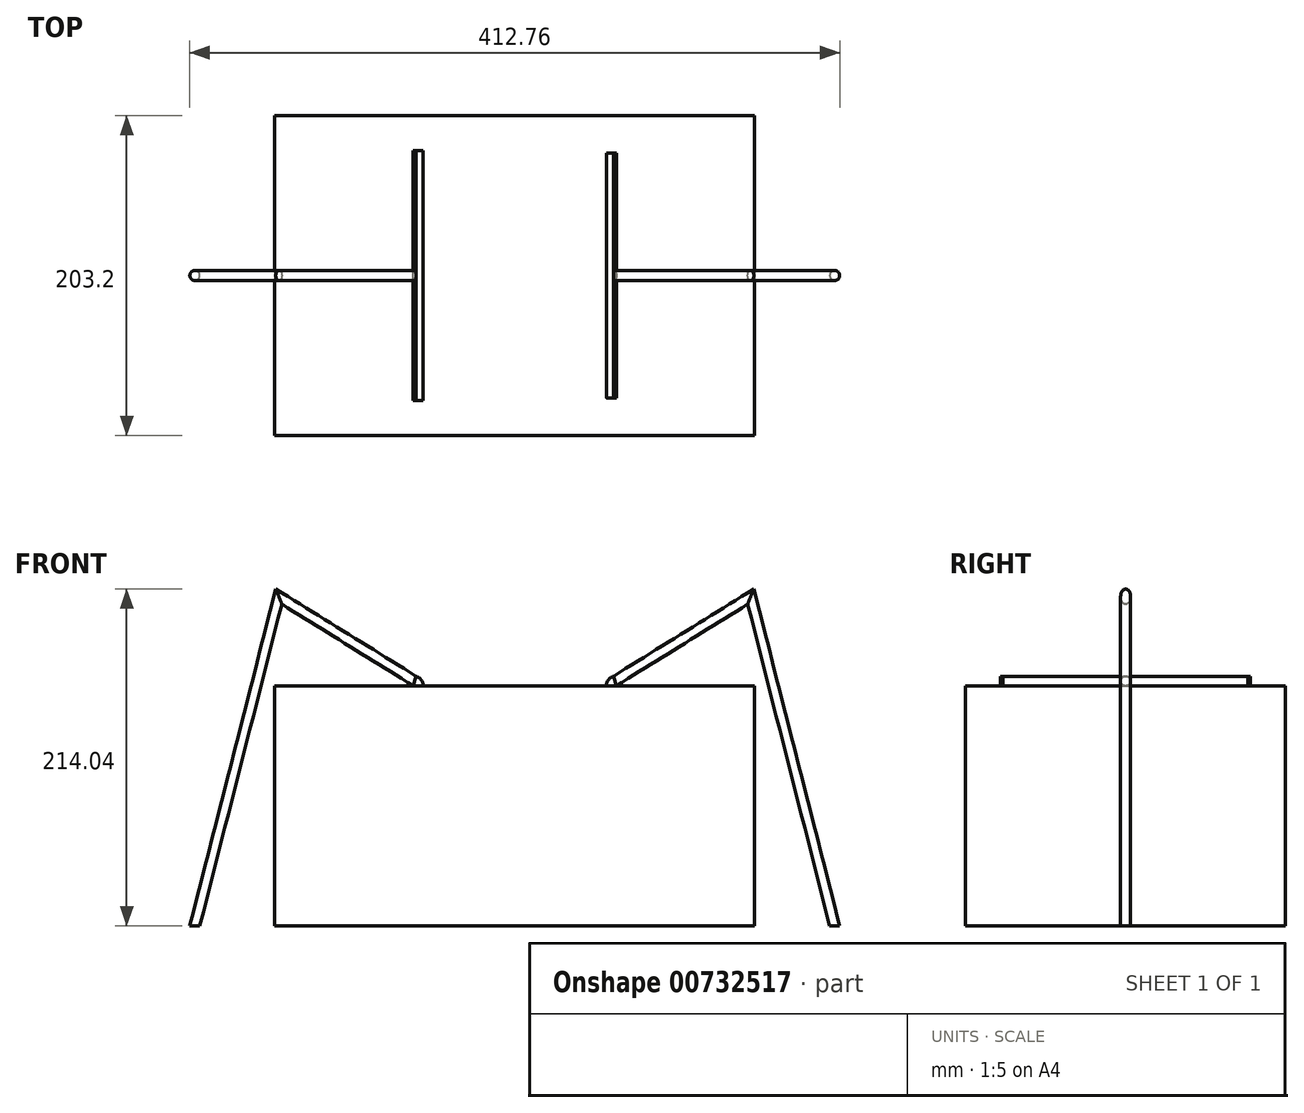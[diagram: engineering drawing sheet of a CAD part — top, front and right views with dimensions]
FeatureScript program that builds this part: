
annotation { "Feature Type Name" : "Feature", "Feature Type Description" : "" }
export const myFeature = defineFeature(function(context is Context, id is Id, definition is map)
    precondition{}
    {
        {
            var Q0;
            Q0=qCreatedBy(makeId("Front.planeOp"),FACE);
            var sketch = newSketch(context, id + "F0", { "sketchPlane" : qUnion([Q0])});
            skLineSegment(sketch, "E0", {"start": v(-152.4, 0) * mm, "end": v(152.4, 0) * mm});
            skLineSegment(sketch, "E1", {"start": v(152.4, 0) * mm, "end": v(152.4, 152.4) * mm});
            skLineSegment(sketch, "E2", {"start": v(152.4, 152.4) * mm, "end": v(-152.4, 152.4) * mm});
            skLineSegment(sketch, "E3", {"start": v(-152.4, 152.4) * mm, "end": v(-152.4, 0) * mm});
            skSolve(sketch);
        }
        {
            var Q0;
            Q0=makeQuery(id+"F0.imprint","IMPRINT",FACE,{"disambiguationData":[TD([[makeQuery(id+"F0.imprint","IMPRINT",EDGE,{"derivedFrom":sQuery(id+"F0.wireOp",EDGE,"E0")}),1.0]])]});
            extrude(context, id + "F1", {"entities" : qUnion([Q0]), "oppositeDirection" : true, "depth" : 203.2 * mm, "offsetDistance" : 25.4 * mm});
        }
        {
            var Q0;
            Q0=qCreatedBy(makeId("Front.planeOp"),FACE);
            cPlane(context, id + "F2", {"entities" : qUnion([Q0]), "cplaneType" : CPlaneType.OFFSET, "offset" : 101.6 * mm, "oppositeDirection" : true, "width" : 152.4 * mm, "height" : 152.4 * mm});
        }
        {
            var Q0;
            Q0=qCreatedBy(id+"F2.planeOp",FACE);
            var sketch = newSketch(context, id + "F3", { "sketchPlane" : qUnion([Q0])});
            skLineSegment(sketch, "E4", {"start": v(-203.2, 0) * mm, "end": v(-149.87, 209.21) * mm});
            skLineSegment(sketch, "E5", {"start": v(-149.87, 209.21) * mm, "end": v(-63.58, 155.58) * mm});
            skLineSegment(sketch, "E6", {"start": v(513.94, 155.57) * mm, "end": v(-315.3, 155.57) * mm, "construction": true});
            skLineSegment(sketch, "E7", {"start": v(203.2, 0) * mm, "end": v(149.87, 209.21) * mm});
            skLineSegment(sketch, "E8", {"start": v(149.87, 209.21) * mm, "end": v(63.58, 155.58) * mm});
            skLineSegment(sketch, "E9", {"start": v(-264.25, 0) * mm, "end": v(372.72, 0) * mm, "construction": true});
            skLineSegment(sketch, "E10.0", {"start": v(-152.4, 152.4) * mm, "end": v(-152.4, 0) * mm, "construction": true});
            skLineSegment(sketch, "E11", {"start": v(-63.5, 155.57) * mm, "end": v(-63.5, 0) * mm, "construction": true});
            skLineSegment(sketch, "E12", {"start": v(63.5, 155.57) * mm, "end": v(63.5, 0) * mm, "construction": true});
            skLineSegment(sketch, "E13.0", {"start": v(152.4, 0) * mm, "end": v(152.4, 152.4) * mm, "construction": true});
            skSolve(sketch);
        }
        {
            var Q0;
            Q0=qCreatedBy(makeId("Top.planeOp"),FACE);
            var sketch = newSketch(context, id + "F4", { "sketchPlane" : qUnion([Q0])});
            skPoint(sketch, "E14.0", {"position": v(-203.2, 101.6) * mm});
            skPoint(sketch, "E15.0", {"position": v(203.2, 101.6) * mm});
            skCircle(sketch, "E16", {"center": v(-203.2, 101.6) * mm, "radius": 3.18 * mm});
            skCircle(sketch, "E17", {"center": v(203.2, 101.6) * mm, "radius": 3.18 * mm});
            skSolve(sketch);
        }
        {
            var Q0;
            Q0=makeQuery(id+"F4.imprint","IMPRINT",FACE,{"disambiguationData":[TD([[makeQuery(id+"F4.imprint","IMPRINT",EDGE,{"derivedFrom":sQuery(id+"F4.wireOp",EDGE,"E16")}),1.0]])]});
            var Q1;
            Q1=sQuery(id+"F3.wireOp",EDGE,"E4");
            var Q2;
            Q2=sQuery(id+"F3.wireOp",EDGE,"E5");
            sweep(context, id + "F5", {"operationType" : NewBodyOperationType.ADD, "profiles" : qUnion([Q0]), "path" : qUnion([Q1, Q2])});
        }
        {
            var Q0;
            Q0=makeQuery(id+"F4.imprint","IMPRINT",FACE,{"disambiguationData":[TD([[makeQuery(id+"F4.imprint","IMPRINT",EDGE,{"derivedFrom":sQuery(id+"F4.wireOp",EDGE,"E17")}),1.0]])]});
            var Q1;
            Q1=sQuery(id+"F3.wireOp",EDGE,"E7");
            var Q2;
            Q2=sQuery(id+"F3.wireOp",EDGE,"E8");
            sweep(context, id + "F6", {"operationType" : NewBodyOperationType.ADD, "profiles" : qUnion([Q0]), "path" : qUnion([Q1, Q2])});
        }
        {
            var Q0;
            Q0=makeQuery(id+"F5.opSweep","CAP_FACE",FACE,{"disambiguationData":[OSD([sQuery(id+"F3.wireOp",VERTEX,"E5.end"),sQuery(id+"F4.wireOp",EDGE,"E16")])],"isStart":false});
            var sketch = newSketch(context, id + "F7", { "sketchPlane" : qUnion([Q0])});
            skCircle(sketch, "E18.0", {"center": v(101.6, 129.13) * mm, "radius": 3.18 * mm, "construction": true});
            skLineSegment(sketch, "E19", {"start": v(104.77, 129.13) * mm, "end": v(98.42, 129.13) * mm, "construction": true});
            skLineSegment(sketch, "E20", {"start": v(101.6, 132.3) * mm, "end": v(101.6, 125.96) * mm, "construction": true});
            skLineSegment(sketch, "E21.bottom", {"start": v(25.4, 125.96) * mm, "end": v(177.8, 125.96) * mm});
            skLineSegment(sketch, "E21.top", {"start": v(25.4, 132.3) * mm, "end": v(177.8, 132.3) * mm});
            skArc(sketch, "E22", {"start": v(25.4, 132.3) * mm, "mid": v(22.22, 129.13) * mm, "end": v(25.4, 125.96) * mm});
            skArc(sketch, "E23", {"start": v(177.8, 125.96) * mm, "mid": v(180.98, 129.13) * mm, "end": v(177.8, 132.3) * mm});
            skLineSegment(sketch, "E24", {"start": v(78.12, 129.13) * mm, "end": v(52.83, 129.13) * mm, "construction": true});
            skSolve(sketch);
        }
        {
            var Q0;
            Q0=qCreatedBy(id+"F2.planeOp",FACE);
            var sketch = newSketch(context, id + "F8", { "sketchPlane" : qUnion([Q0])});
            skLineSegment(sketch, "E25.0", {"start": v(-62.63, 158.6) * mm, "end": v(-64.54, 152.55) * mm});
            skArc(sketch, "E26", {"start": v(-58.2, 152.55) * mm, "mid": v(-59.42, 156.3) * mm, "end": v(-62.63, 158.6) * mm});
            skLineSegment(sketch, "E27", {"start": v(-64.54, 152.55) * mm, "end": v(-58.2, 152.55) * mm});
            skSolve(sketch);
        }
        {
            var Q0;
            Q0=makeQuery(id+"F8.imprint","IMPRINT",FACE,{"disambiguationData":[TD([[makeQuery(id+"F8.imprint","IMPRINT",EDGE,{"derivedFrom":sQuery(id+"F8.wireOp",EDGE,"E25.0")}),1.0]])]});
            var Q1;
            Q1=sQuery(id+"F8.wireOp",EDGE,"E26");
            var Q2;
            Q2=sQuery(id+"F8.wireOp",EDGE,"E27");
            var Q3;
            Q3=sQuery(id+"F8.wireOp",EDGE,"E25.0");
            extrude(context, id + "F9", {"entities" : qUnion([Q0]), "operationType" : NewBodyOperationType.ADD, "surfaceEntities" : qUnion([Q1, Q2, Q3]), "depth" : 158.75 * mm, "offsetDistance" : 25.4 * mm, "symmetric" : true});
        }
        {
            var Q0;
            Q0=qCreatedBy(id+"F2.planeOp",FACE);
            var sketch = newSketch(context, id + "F10", { "sketchPlane" : qUnion([Q0])});
            skLineSegment(sketch, "E28.0", {"start": v(64.54, 152.55) * mm, "end": v(62.63, 158.6) * mm});
            skLineSegment(sketch, "E29", {"start": v(64.54, 152.55) * mm, "end": v(58.2, 152.55) * mm});
            skArc(sketch, "E30", {"start": v(62.63, 158.6) * mm, "mid": v(59.42, 156.3) * mm, "end": v(58.2, 152.55) * mm});
            skSolve(sketch);
        }
        {
            var Q0;
            Q0=makeQuery(id+"F10.imprint","IMPRINT",FACE,{"disambiguationData":[TD([[makeQuery(id+"F10.imprint","IMPRINT",EDGE,{"derivedFrom":sQuery(id+"F10.wireOp",EDGE,"E28.0")}),1.0]])]});
            extrude(context, id + "F11", {"entities" : qUnion([Q0]), "operationType" : NewBodyOperationType.ADD, "depth" : 155.57 * mm, "offsetDistance" : 25.4 * mm, "symmetric" : true});
        }
    });
